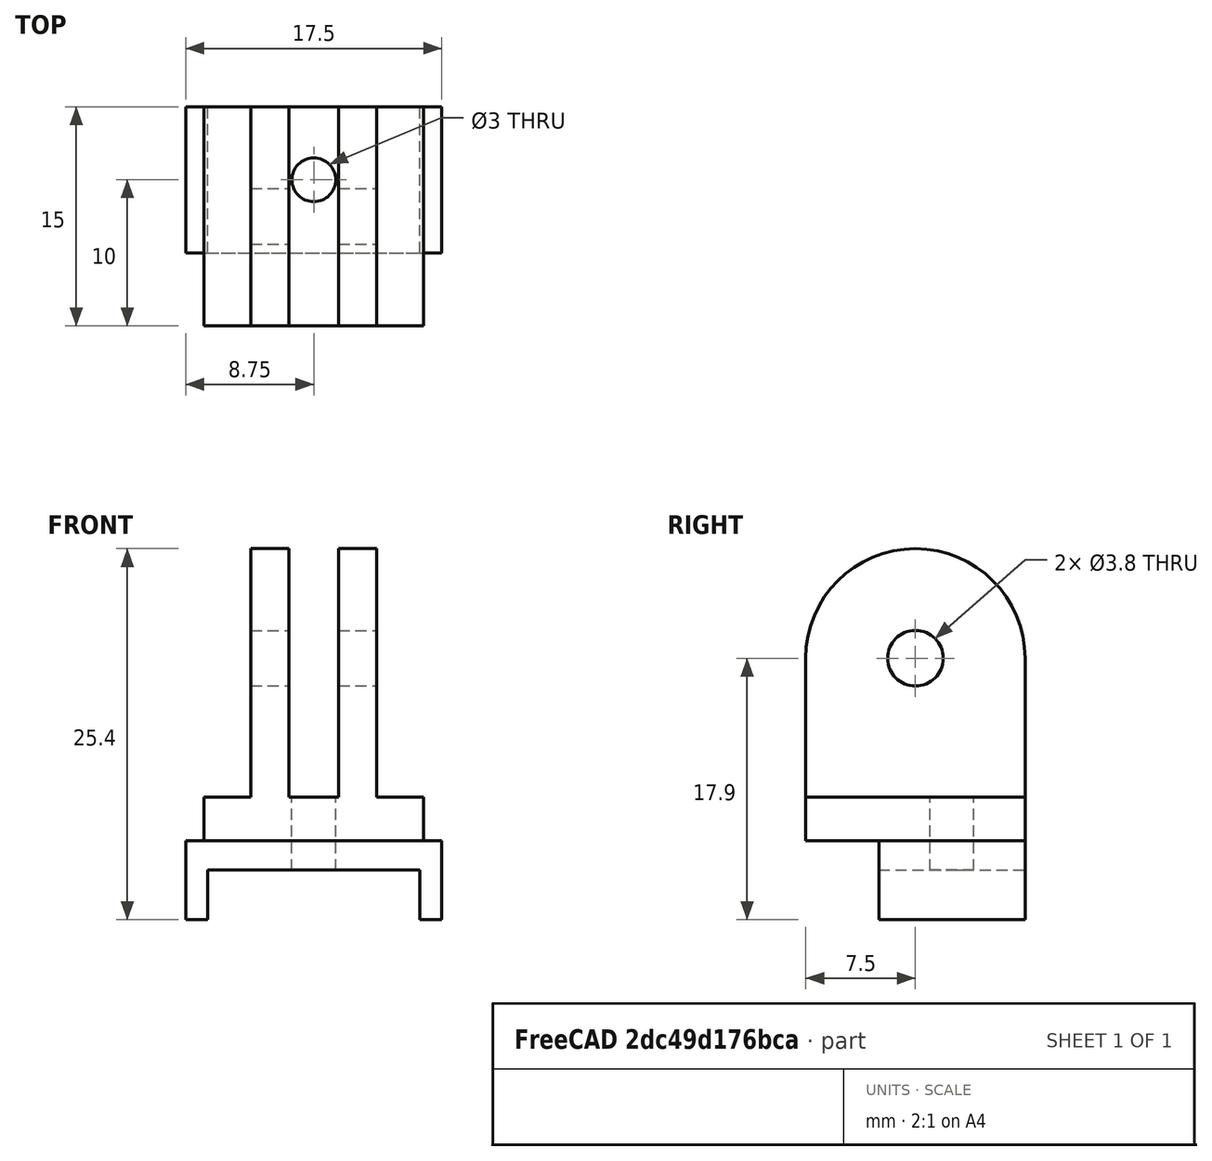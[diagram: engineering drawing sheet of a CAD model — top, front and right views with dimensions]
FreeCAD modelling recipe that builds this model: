
FCSTD DOCUMENT  (FreeCAD 0.19R23578 (Git))
Label: light_sensor_lm393
License: FreeArt
LicenseURL: http://artlibre.org/licence/lal
objects: Part::Box×2, Part::Cut×2, Spreadsheet::Sheet×1, Part::Feature×1, Part::Cylinder×1, Part::MultiFuse×1, App::Part×1
note: 7 computed .brp shape members not serialized (recipe doc carries the construction recipe); baked Part::Feature solids carry a one-line shape summary decoded from their .brp

FEATURE [Part::Box] Box008  label="pcb holder cube"
  AttacherType = Attacher::AttachEngine3D
  Height = 5.4
  Length = 17.5
  Width = 10
  expr: Width = <<p>>.pcb_holder_y
  expr: Height = <<p>>.pcb_holder_z + <<p>>.pcb_z + <<p>>.pcb_above
  expr: Length = <<p>>.pcb_x + 2 * <<p>>.side_wall
FEATURE [Spreadsheet::Sheet] Spreadsheet001  label="p"
  cells = A1=pcb_x; B1(pcb_x)=14.5; A2=pcb_y; B2(pcb_y)=32; A3=pcb_z; B3(pcb_z)=1.4; A4=pcb_holder_y; B4(pcb_holder_y)=10; A5=pcb_holder_z; B5(pcb_holder_z)=2; A6=pcb_above; B6(pcb_above)=2; A7=hole_dist_x; B7(hole_dist_x)=6.5; A8=hole_off_y; B8(hole_off_y)=2.5; A9=hole_r; B9(hole_r)=1.5; A10=side_wall; B10(side_wall)=1.5
FEATURE [Part::Feature] Cut001001  label="side 2 cut"
  Placement = pos=(0,0,5.4) rot=(0,0,1;1.5708rad)
  shape: bbox 15 x 15 x 20 mm, 16 faces (baked)
  expr: .Placement.Base.z = <<p>>.pcb_z + <<p>>.pcb_holder_z + <<p>>.pcb_above
FEATURE [Part::Box] Box009  label="pcb holder extract"
  AttacherType = Attacher::AttachEngine3D
  Height = 3.4
  Length = 14.5
  Placement = pos=(1.5,0,0) rot=(0,0,1;0rad)
  Width = 10
  expr: .Placement.Base.x = <<p>>.side_wall
  expr: Length = <<p>>.pcb_x
  expr: Height = <<p>>.pcb_z + <<p>>.pcb_above
  expr: Width = <<p>>.pcb_holder_y
FEATURE [Part::Cylinder] Cylinder001  label="screw hole"
  Angle = 360
  AttacherType = Attacher::AttachEngine3D
  Height = 10
  Placement = pos=(0,2.5,0) rot=(0,0,1;0rad)
  Radius = 1.5
  expr: .Placement.Base.y = <<p>>.pcb_holder_y - 15 / 2
  expr: Radius = <<p>>.hole_r
FEATURE [Part::Cut] Cut  label="pcb holder cut"
  Base = -> Box008
  Placement = pos=(-8.75,-2.5,0) rot=(0,0,1;0rad)
  Tool = -> Box009
  expr: .Placement.Base.y = -(15 - <<p>>.pcb_holder_y) / 2
  expr: .Placement.Base.x = -(<<p>>.pcb_x + 2 * <<p>>.side_wall) / 2
FEATURE [Part::MultiFuse] Fusion  label="body fusion"
  Shapes = -> [Cut001001,Cut]
FEATURE [Part::Cut] Cut001002  label="body cut"
  Base = -> Fusion
  Tool = -> Cylinder001
FEATURE [App::Part] Part  label="pcb box part"
  Group = -> [Cut001001,Box009,Box008,Cut,Fusion,Cylinder001,Cut001002]
  Origin = -> Origin
